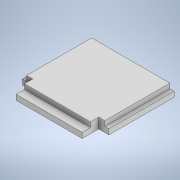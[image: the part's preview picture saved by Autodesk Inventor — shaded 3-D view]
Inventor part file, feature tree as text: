
AUTODESK INVENTOR PART (.ipt)
format: ipt  version: 2020 (Build 240168000, 168)  size: 282,624 bytes
history: native  units: in
note: dims shown in document units (in); Inventor stores cm internally (conversion verified against a paired STEP export)
features: extrude x4, sketch x4
ambient origin geometry x8: Origin, YZ Plane, XZ Plane, XY Plane, X Axis, Y Axis, Z Axis, Center Point
bodies: Body1 (feature_tree)
feature tree (8):
  extrude  "Extrusion4"  Depth=1.05in
  extrude  "Extrusion5"  Depth=0.05in
  extrude  "Extrusion8"  Depth=0.05in
  extrude  "Extrusion9"  Depth=0.8in
  sketch  "Sketch4"  dims[d20=0.79in d21=1.05in]
  sketch  "Sketch5"  dims[d22=0.065in d23=0.0in d24=0.05in]
  sketch  "Sketch8"  dims[d25=0.0in d26=0.05in]
  sketch  "Sketch9"  dims[d27=0.06in d28=0.0in d42=0.8in d43=0.065in d44=0.0in d45=1.05in d46=0.125in d47=0.2in d48=0.0in d49=0.06in d50=0.0in d51=0.5in d52=0.0344in d53=0.5in d54=0.0344in]
